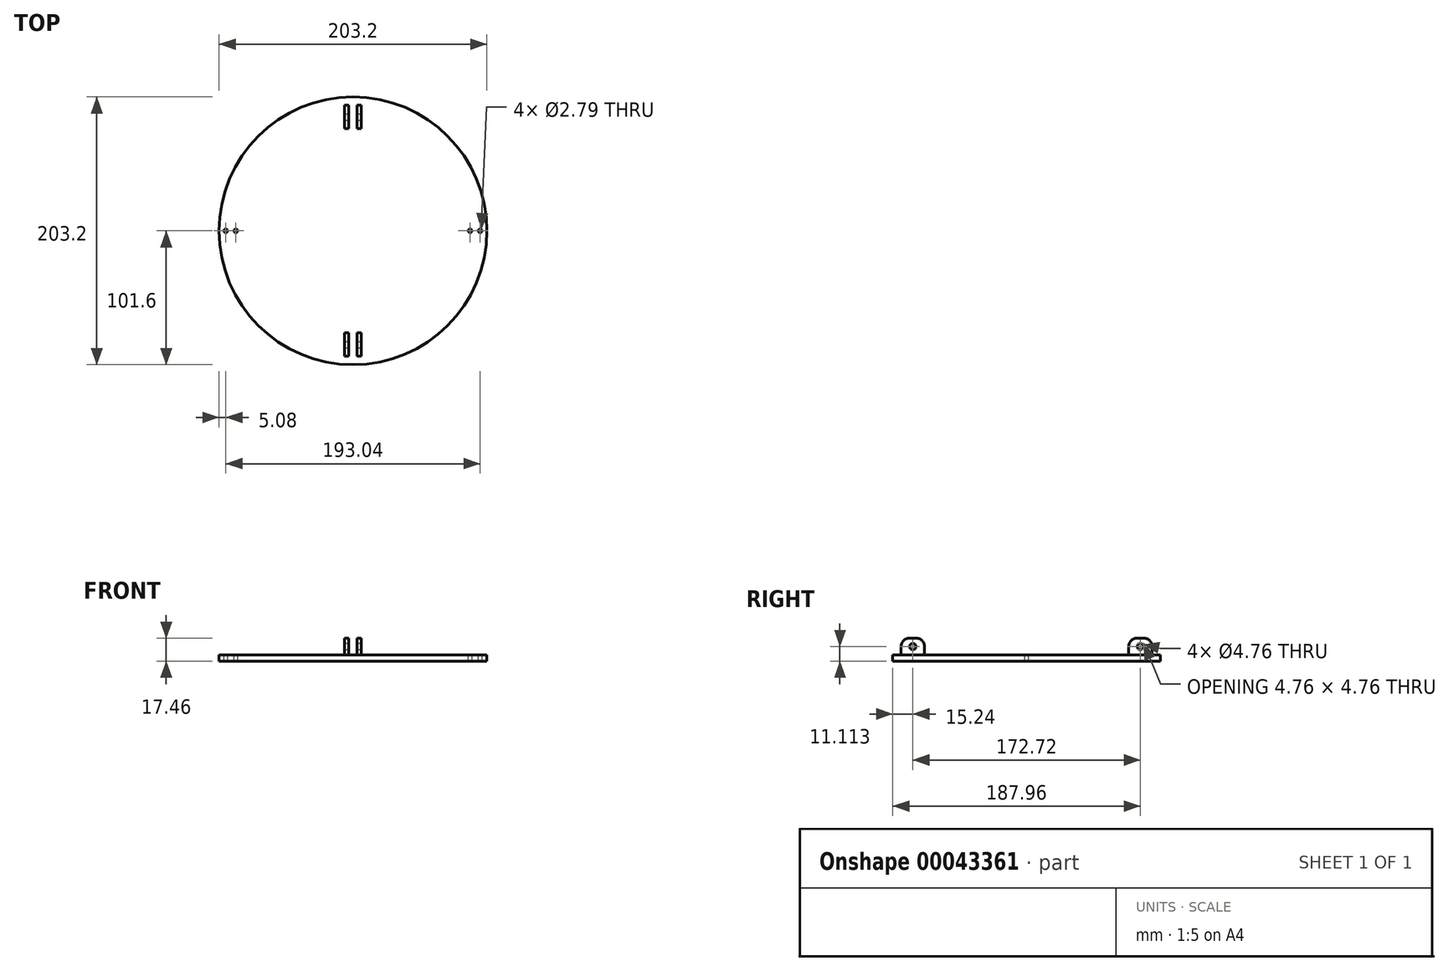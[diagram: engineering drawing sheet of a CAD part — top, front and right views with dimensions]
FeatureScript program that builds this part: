
annotation { "Feature Type Name" : "Feature", "Feature Type Description" : "" }
export const myFeature = defineFeature(function(context is Context, id is Id, definition is map)
    precondition{}
    {
        {
            var Q0;
            Q0=qCreatedBy(makeId("Top.planeOp"),FACE);
            var sketch = newSketch(context, id + "F0", { "sketchPlane" : qUnion([Q0])});
            skLineSegment(sketch, "E0.rect.bottom", {"start": v(-101.6, 101.6) * mm, "end": v(101.6, 101.6) * mm});
            skLineSegment(sketch, "E0.rect.top", {"start": v(-101.6, -101.6) * mm, "end": v(101.6, -101.6) * mm});
            skLineSegment(sketch, "E0.rect.left", {"start": v(-101.6, 101.6) * mm, "end": v(-101.6, -101.6) * mm});
            skLineSegment(sketch, "E0.rect.right", {"start": v(101.6, 101.6) * mm, "end": v(101.6, -101.6) * mm});
            skPoint(sketch, "E0.rect.middle", {"position": v(0, 0) * mm});
            skSolve(sketch);
        }
        {
            var Q0;
            Q0=qSketchRegion(id+"F0",true);
            extrude(context, id + "F1", {"entities" : qUnion([Q0]), "depth" : 4.76 * mm});
        }
        {
            var Q0;
            Q0=qCreatedBy(makeId("Right.planeOp"),FACE);
            var sketch = newSketch(context, id + "F2", { "sketchPlane" : qUnion([Q0])});
            skLineSegment(sketch, "E1.bottom", {"start": v(95.25, 4.76) * mm, "end": v(77.47, 4.76) * mm});
            skLineSegment(sketch, "E1.top", {"start": v(95.25, 17.46) * mm, "end": v(77.47, 17.46) * mm});
            skLineSegment(sketch, "E1.left", {"start": v(95.25, 4.76) * mm, "end": v(95.25, 17.46) * mm});
            skLineSegment(sketch, "E1.right", {"start": v(77.47, 4.76) * mm, "end": v(77.47, 17.46) * mm});
            skLineSegment(sketch, "E2", {"start": v(0, 0) * mm, "end": v(0, -24.95) * mm, "construction": true});
            skLineSegment(sketch, "E3.MirrorCS", {"start": v(-95.25, 17.46) * mm, "end": v(-77.47, 17.46) * mm});
            skLineSegment(sketch, "E4.MirrorCS", {"start": v(-95.25, 4.76) * mm, "end": v(-95.25, 17.46) * mm});
            skLineSegment(sketch, "E5.MirrorCS", {"start": v(-77.47, 4.76) * mm, "end": v(-77.47, 17.46) * mm});
            skLineSegment(sketch, "E6.MirrorCS", {"start": v(-95.25, 4.76) * mm, "end": v(-77.47, 4.76) * mm});
            skSolve(sketch);
        }
        {
            var Q0;
            Q0=makeQuery(id+"F2.imprint","IMPRINT",FACE,{"disambiguationData":[TD([[makeQuery(id+"F2.imprint","IMPRINT",EDGE,{"derivedFrom":sQuery(id+"F2.wireOp",EDGE,"E3.MirrorCS")}),-1.0]])]});
            var Q1;
            Q1=makeQuery(id+"F2.imprint","IMPRINT",FACE,{"disambiguationData":[TD([[makeQuery(id+"F2.imprint","IMPRINT",EDGE,{"derivedFrom":sQuery(id+"F2.wireOp",EDGE,"E1.bottom")}),-1.0]])]});
            extrude(context, id + "F3", {"entities" : qUnion([Q0, Q1]), "operationType" : NewBodyOperationType.ADD, "endBound" : BoundingType.SYMMETRIC, "depth" : 12.7 * mm});
        }
        {
            var Q0;
            Q0=makeQuery(id+"F3.opExtrude","SWEPT_FACE",FACE,{"disambiguationData":[OSD([sQuery(id+"F2.wireOp",EDGE,"E3.MirrorCS")])]});
            var sketch = newSketch(context, id + "F4", { "sketchPlane" : qUnion([Q0])});
            skLineSegment(sketch, "E7.bottom", {"start": v(-3.17, -95.25) * mm, "end": v(3.18, -95.25) * mm});
            skLineSegment(sketch, "E7.top", {"start": v(-3.17, -77.47) * mm, "end": v(3.18, -77.47) * mm});
            skLineSegment(sketch, "E7.left", {"start": v(-3.17, -95.25) * mm, "end": v(-3.17, -77.47) * mm});
            skLineSegment(sketch, "E7.right", {"start": v(3.18, -95.25) * mm, "end": v(3.18, -77.47) * mm});
            skLineSegment(sketch, "E8", {"start": v(0, -95.25) * mm, "end": v(0, -77.47) * mm, "construction": true});
            skLineSegment(sketch, "E9", {"start": v(0, 0) * mm, "end": v(15.83, 0) * mm, "construction": true});
            skLineSegment(sketch, "E10.MirrorCS", {"start": v(3.18, -95.25) * mm, "end": v(-3.17, -95.25) * mm});
            skLineSegment(sketch, "E11.MirrorCS", {"start": v(3.18, -77.47) * mm, "end": v(-3.17, -77.47) * mm});
            skLineSegment(sketch, "E12.MirrorCS", {"start": v(-3.17, 77.47) * mm, "end": v(3.18, 77.47) * mm});
            skLineSegment(sketch, "E13.MirrorCS", {"start": v(-3.17, 95.25) * mm, "end": v(3.18, 95.25) * mm});
            skLineSegment(sketch, "E14.MirrorCS", {"start": v(3.18, 95.25) * mm, "end": v(-3.17, 95.25) * mm});
            skLineSegment(sketch, "E15.MirrorCS", {"start": v(3.18, 77.47) * mm, "end": v(-3.17, 77.47) * mm});
            skLineSegment(sketch, "E16.MirrorCS", {"start": v(3.18, 95.25) * mm, "end": v(3.18, 77.47) * mm});
            skLineSegment(sketch, "E17.MirrorCS", {"start": v(-3.17, 95.25) * mm, "end": v(-3.17, 77.47) * mm});
            skLineSegment(sketch, "E18.MirrorCS", {"start": v(0, 95.25) * mm, "end": v(0, 77.47) * mm});
            skSolve(sketch);
        }
        {
            var Q0;
            Q0 = qSketchRegion(id + "F4", true);
            var Q1;
            Q1=makeQuery(id+"F1.opExtrude","CAP_FACE",FACE,{"disambiguationData":[OSD([sQuery(id+"F0.wireOp",EDGE,"E0.rect.bottom"),sQuery(id+"F0.wireOp",EDGE,"E0.rect.top"),sQuery(id+"F0.wireOp",EDGE,"E0.rect.left"),sQuery(id+"F0.wireOp",EDGE,"E0.rect.right")])],"isStart":false});
            extrude(context, id + "F5", {"entities" : qUnion([Q0]), "operationType" : NewBodyOperationType.REMOVE, "endBound" : BoundingType.UP_TO_SURFACE, "oppositeDirection" : true, "endBoundEntityFace" : qUnion([Q1]), "depth" : 25.4 * mm});
        }
        {
            var Q0;
            Q0=makeQuery(id+"F3.opExtrude","CAP_FACE",FACE,{"disambiguationData":[OSD([sQuery(id+"F2.wireOp",EDGE,"E3.MirrorCS"),sQuery(id+"F2.wireOp",EDGE,"E4.MirrorCS"),sQuery(id+"F2.wireOp",EDGE,"E5.MirrorCS"),sQuery(id+"F2.wireOp",EDGE,"E6.MirrorCS")])],"isStart":false});
            var sketch = newSketch(context, id + "F6", { "sketchPlane" : qUnion([Q0])});
            skLineSegment(sketch, "E19", {"start": v(-95.25, 4.76) * mm, "end": v(-77.47, 17.46) * mm});
            skLineSegment(sketch, "E20", {"start": v(77.47, 17.46) * mm, "end": v(95.25, 4.76) * mm});
            skPoint(sketch, "E21", {"position": v(86.36, 11.11) * mm});
            skPoint(sketch, "E22", {"position": v(-86.36, 11.11) * mm});
            skSolve(sketch);
        }
        {
            var Q0;
            Q0=sQuery(id+"F6.wireOp",VERTEX,"E22");
            var Q1;
            Q1=sQuery(id+"F6.wireOp",VERTEX,"E21");
            var Q2;
            Q2=makeQuery(id+"F1.opExtrude","SWEPT_BODY",BODY,{"disambiguationData":[OSD([sQuery(id+"F0.wireOp",EDGE,"E0.rect.bottom"),sQuery(id+"F0.wireOp",EDGE,"E0.rect.top"),sQuery(id+"F0.wireOp",EDGE,"E0.rect.left"),sQuery(id+"F0.wireOp",EDGE,"E0.rect.right")])]});
            hole(context, id + "F7", {"style" : HoleStyle.SIMPLE, "holeDiameter" : 4.76 * mm, "endStyle" : HoleEndStyle.THROUGH, "locations" : qUnion([Q0, Q1]), "scope" : qUnion([Q2])});
        }
        {
            var Q0;
            Q0=makeQuery(id+"F5.boolean.opBoolean","MERGE",FACE,{"derivedFrom":[makeQuery(id+"F1.opExtrude","CAP_FACE",FACE,{"disambiguationData":[OSD([sQuery(id+"F0.wireOp",EDGE,"E0.rect.bottom"),sQuery(id+"F0.wireOp",EDGE,"E0.rect.top"),sQuery(id+"F0.wireOp",EDGE,"E0.rect.left"),sQuery(id+"F0.wireOp",EDGE,"E0.rect.right")])],"isStart":false}),makeQuery(id+"F5.opExtrude","CAP_FACE",FACE,{"disambiguationData":[OSD([sQuery(id+"F4.wireOp",EDGE,"E10.MirrorCS"),sQuery(id+"F4.wireOp",EDGE,"E7.top"),sQuery(id+"F4.wireOp",EDGE,"E7.right"),sQuery(id+"F4.wireOp",EDGE,"E7.left")])],"isStart":false}),makeQuery(id+"F5.opExtrude","CAP_FACE",FACE,{"disambiguationData":[OSD([sQuery(id+"F4.wireOp",EDGE,"E15.MirrorCS"),sQuery(id+"F4.wireOp",EDGE,"E13.MirrorCS"),sQuery(id+"F4.wireOp",EDGE,"E16.MirrorCS"),sQuery(id+"F4.wireOp",EDGE,"E17.MirrorCS")])],"isStart":false})]});
            var sketch = newSketch(context, id + "F8", { "sketchPlane" : qUnion([Q0])});
            skCircle(sketch, "E23", {"center": v(0, 0) * mm, "radius": 101.6 * mm});
            skSolve(sketch);
        }
        {
            var Q0;
            {var subQ0=makeQuery(id+"F1.opExtrude","CAP_EDGE",EDGE,{"disambiguationData":[OSD([sQuery(id+"F0.wireOp",EDGE,"E0.rect.left")])],"isStart":false});var subQ1=sQuery(id+"F8.wireOp",EDGE,"E23");var subQ2=makeQuery(id+"F8.imprint","INTERSECT",VERTEX,{"derivedFrom":[subQ0,subQ1]});Q0=makeQuery(id+"F8.imprint","IMPRINT",FACE,{"disambiguationData":[TD([[makeQuery(id+"F8.imprint","IMPRINT",EDGE,{"disambiguationData":[TD([[subQ2,-1.0]])],"derivedFrom":subQ1}),-1.0]])]});}
            var Q1;
            {var subQ1=sQuery(id+"F8.wireOp",EDGE,"E23");var subQ3=makeQuery(id+"F1.opExtrude","CAP_EDGE",EDGE,{"disambiguationData":[OSD([sQuery(id+"F0.wireOp",EDGE,"E0.rect.bottom")])],"isStart":false});var subQ5=makeQuery(id+"F8.imprint","INTERSECT",VERTEX,{"derivedFrom":[subQ3,subQ1]});Q1=makeQuery(id+"F8.imprint","IMPRINT",FACE,{"disambiguationData":[TD([[makeQuery(id+"F8.imprint","IMPRINT",EDGE,{"disambiguationData":[TD([[subQ5,-1.0]])],"derivedFrom":subQ1}),-1.0]])]});}
            var Q2;
            {var subQ0=makeQuery(id+"F1.opExtrude","CAP_EDGE",EDGE,{"disambiguationData":[OSD([sQuery(id+"F0.wireOp",EDGE,"E0.rect.bottom")])],"isStart":false});var subQ1=sQuery(id+"F8.wireOp",EDGE,"E23");var subQ2=makeQuery(id+"F8.imprint","INTERSECT",VERTEX,{"derivedFrom":[subQ0,subQ1]});Q2=makeQuery(id+"F8.imprint","IMPRINT",FACE,{"disambiguationData":[TD([[makeQuery(id+"F8.imprint","IMPRINT",EDGE,{"disambiguationData":[TD([[subQ2,1.0]])],"derivedFrom":subQ1}),-1.0]])]});}
            var Q3;
            {var subQ0=makeQuery(id+"F1.opExtrude","CAP_EDGE",EDGE,{"disambiguationData":[OSD([sQuery(id+"F0.wireOp",EDGE,"E0.rect.right")])],"isStart":false});var subQ1=sQuery(id+"F8.wireOp",EDGE,"E23");var subQ2=makeQuery(id+"F8.imprint","INTERSECT",VERTEX,{"derivedFrom":[subQ0,subQ1]});Q3=makeQuery(id+"F8.imprint","IMPRINT",FACE,{"disambiguationData":[TD([[makeQuery(id+"F8.imprint","IMPRINT",EDGE,{"disambiguationData":[TD([[subQ2,1.0]])],"derivedFrom":subQ1}),-1.0]])]});}
            extrude(context, id + "F9", {"entities" : qUnion([Q0, Q1, Q2, Q3]), "operationType" : NewBodyOperationType.REMOVE, "endBound" : BoundingType.THROUGH_ALL, "oppositeDirection" : true, "depth" : 25.4 * mm});
        }
        {
            var Q0;
            {var subQ0=sQuery(id+"F2.wireOp",EDGE,"E3.MirrorCS");var subQ1=sQuery(id+"F2.wireOp",EDGE,"E4.MirrorCS");Q0=makeQuery(id+"F5.boolean.opBoolean","SPLIT",EDGE,{"disambiguationData":[TD([makeQuery(id+"F5.opExtrude","SWEPT_FACE",FACE,{"disambiguationData":[OSD([sQuery(id+"F4.wireOp",EDGE,"E7.left")])]})])],"derivedFrom":makeQuery(id+"F3.opExtrude","SWEPT_EDGE",EDGE,{"disambiguationData":[OSD([subQ0,subQ1])]})});}
            var Q1;
            {var subQ0=sQuery(id+"F2.wireOp",EDGE,"E3.MirrorCS");var subQ1=sQuery(id+"F2.wireOp",EDGE,"E5.MirrorCS");Q1=makeQuery(id+"F5.boolean.opBoolean","SPLIT",EDGE,{"disambiguationData":[TD([makeQuery(id+"F5.opExtrude","SWEPT_FACE",FACE,{"disambiguationData":[OSD([sQuery(id+"F4.wireOp",EDGE,"E7.left")])]})])],"derivedFrom":makeQuery(id+"F3.opExtrude","SWEPT_EDGE",EDGE,{"disambiguationData":[OSD([subQ0,subQ1])]})});}
            var Q2;
            {var subQ0=sQuery(id+"F2.wireOp",EDGE,"E1.top");var subQ1=sQuery(id+"F2.wireOp",EDGE,"E1.right");Q2=makeQuery(id+"F5.boolean.opBoolean","SPLIT",EDGE,{"disambiguationData":[TD([makeQuery(id+"F5.opExtrude","SWEPT_FACE",FACE,{"disambiguationData":[OSD([sQuery(id+"F4.wireOp",EDGE,"E17.MirrorCS")])]})])],"derivedFrom":makeQuery(id+"F3.opExtrude","SWEPT_EDGE",EDGE,{"disambiguationData":[OSD([subQ0,subQ1])]})});}
            var Q3;
            {var subQ0=sQuery(id+"F2.wireOp",EDGE,"E1.top");var subQ1=sQuery(id+"F2.wireOp",EDGE,"E1.left");Q3=makeQuery(id+"F5.boolean.opBoolean","SPLIT",EDGE,{"disambiguationData":[TD([makeQuery(id+"F5.opExtrude","SWEPT_FACE",FACE,{"disambiguationData":[OSD([sQuery(id+"F4.wireOp",EDGE,"E17.MirrorCS")])]})])],"derivedFrom":makeQuery(id+"F3.opExtrude","SWEPT_EDGE",EDGE,{"disambiguationData":[OSD([subQ0,subQ1])]})});}
            var Q4;
            {var subQ0=sQuery(id+"F2.wireOp",EDGE,"E1.top");var subQ1=sQuery(id+"F2.wireOp",EDGE,"E1.left");Q4=makeQuery(id+"F5.boolean.opBoolean","SPLIT",EDGE,{"disambiguationData":[TD([makeQuery(id+"F5.opExtrude","SWEPT_FACE",FACE,{"disambiguationData":[OSD([sQuery(id+"F4.wireOp",EDGE,"E16.MirrorCS")])]})])],"derivedFrom":makeQuery(id+"F3.opExtrude","SWEPT_EDGE",EDGE,{"disambiguationData":[OSD([subQ0,subQ1])]})});}
            var Q5;
            {var subQ0=sQuery(id+"F2.wireOp",EDGE,"E1.top");var subQ1=sQuery(id+"F2.wireOp",EDGE,"E1.right");Q5=makeQuery(id+"F5.boolean.opBoolean","SPLIT",EDGE,{"disambiguationData":[TD([makeQuery(id+"F5.opExtrude","SWEPT_FACE",FACE,{"disambiguationData":[OSD([sQuery(id+"F4.wireOp",EDGE,"E16.MirrorCS")])]})])],"derivedFrom":makeQuery(id+"F3.opExtrude","SWEPT_EDGE",EDGE,{"disambiguationData":[OSD([subQ0,subQ1])]})});}
            var Q6;
            {var subQ0=sQuery(id+"F2.wireOp",EDGE,"E3.MirrorCS");var subQ1=sQuery(id+"F2.wireOp",EDGE,"E4.MirrorCS");Q6=makeQuery(id+"F5.boolean.opBoolean","SPLIT",EDGE,{"disambiguationData":[TD([makeQuery(id+"F5.opExtrude","SWEPT_FACE",FACE,{"disambiguationData":[OSD([sQuery(id+"F4.wireOp",EDGE,"E7.right")])]})])],"derivedFrom":makeQuery(id+"F3.opExtrude","SWEPT_EDGE",EDGE,{"disambiguationData":[OSD([subQ0,subQ1])]})});}
            var Q7;
            {var subQ0=sQuery(id+"F2.wireOp",EDGE,"E3.MirrorCS");var subQ1=sQuery(id+"F2.wireOp",EDGE,"E5.MirrorCS");Q7=makeQuery(id+"F5.boolean.opBoolean","SPLIT",EDGE,{"disambiguationData":[TD([makeQuery(id+"F5.opExtrude","SWEPT_FACE",FACE,{"disambiguationData":[OSD([sQuery(id+"F4.wireOp",EDGE,"E7.right")])]})])],"derivedFrom":makeQuery(id+"F3.opExtrude","SWEPT_EDGE",EDGE,{"disambiguationData":[OSD([subQ0,subQ1])]})});}
            fillet(context, id + "F10", {"entities" : qUnion([Q0, Q1, Q2, Q3, Q4, Q5, Q6, Q7]), "radius" : 6.35 * mm, "tangentPropagation" : true, "allowEdgeOverflow" : false});
        }
        {
            var Q0;
            Q0=makeQuery(id+"F5.boolean.opBoolean","MERGE",FACE,{"derivedFrom":[makeQuery(id+"F1.opExtrude","CAP_FACE",FACE,{"disambiguationData":[OSD([sQuery(id+"F0.wireOp",EDGE,"E0.rect.bottom"),sQuery(id+"F0.wireOp",EDGE,"E0.rect.top"),sQuery(id+"F0.wireOp",EDGE,"E0.rect.left"),sQuery(id+"F0.wireOp",EDGE,"E0.rect.right")])],"isStart":false}),makeQuery(id+"F5.opExtrude","CAP_FACE",FACE,{"disambiguationData":[OSD([sQuery(id+"F4.wireOp",EDGE,"E10.MirrorCS"),sQuery(id+"F4.wireOp",EDGE,"E7.top"),sQuery(id+"F4.wireOp",EDGE,"E7.right"),sQuery(id+"F4.wireOp",EDGE,"E7.left")])],"isStart":false}),makeQuery(id+"F5.opExtrude","CAP_FACE",FACE,{"disambiguationData":[OSD([sQuery(id+"F4.wireOp",EDGE,"E15.MirrorCS"),sQuery(id+"F4.wireOp",EDGE,"E13.MirrorCS"),sQuery(id+"F4.wireOp",EDGE,"E16.MirrorCS"),sQuery(id+"F4.wireOp",EDGE,"E17.MirrorCS")])],"isStart":false})]});
            var sketch = newSketch(context, id + "F11", { "sketchPlane" : qUnion([Q0])});
            skLineSegment(sketch, "E24", {"start": v(-88.9, 0) * mm, "end": v(88.9, 0) * mm});
            skLineSegment(sketch, "E25", {"start": v(-88.9, 0) * mm, "end": v(-96.52, 0) * mm});
            skLineSegment(sketch, "E26", {"start": v(88.9, 0) * mm, "end": v(96.52, 0) * mm});
            skSolve(sketch);
        }
        {
            var Q0;
            Q0=sQuery(id+"F11.wireOp",VERTEX,"E24.start");
            var Q1;
            Q1=sQuery(id+"F11.wireOp",VERTEX,"E24.end");
            var Q2;
            Q2=sQuery(id+"F11.wireOp",VERTEX,"E25.end");
            var Q3;
            Q3=sQuery(id+"F11.wireOp",VERTEX,"E26.end");
            var Q4;
            Q4=makeQuery(id+"F1.opExtrude","SWEPT_BODY",BODY,{"disambiguationData":[OSD([sQuery(id+"F0.wireOp",EDGE,"E0.rect.bottom"),sQuery(id+"F0.wireOp",EDGE,"E0.rect.top"),sQuery(id+"F0.wireOp",EDGE,"E0.rect.left"),sQuery(id+"F0.wireOp",EDGE,"E0.rect.right")])]});
            hole(context, id + "F12", {"style" : HoleStyle.SIMPLE, "holeDiameter" : 2.8 * mm, "endStyle" : HoleEndStyle.THROUGH, "locations" : qUnion([Q0, Q1, Q2, Q3]), "scope" : qUnion([Q4])});
        }
    });
